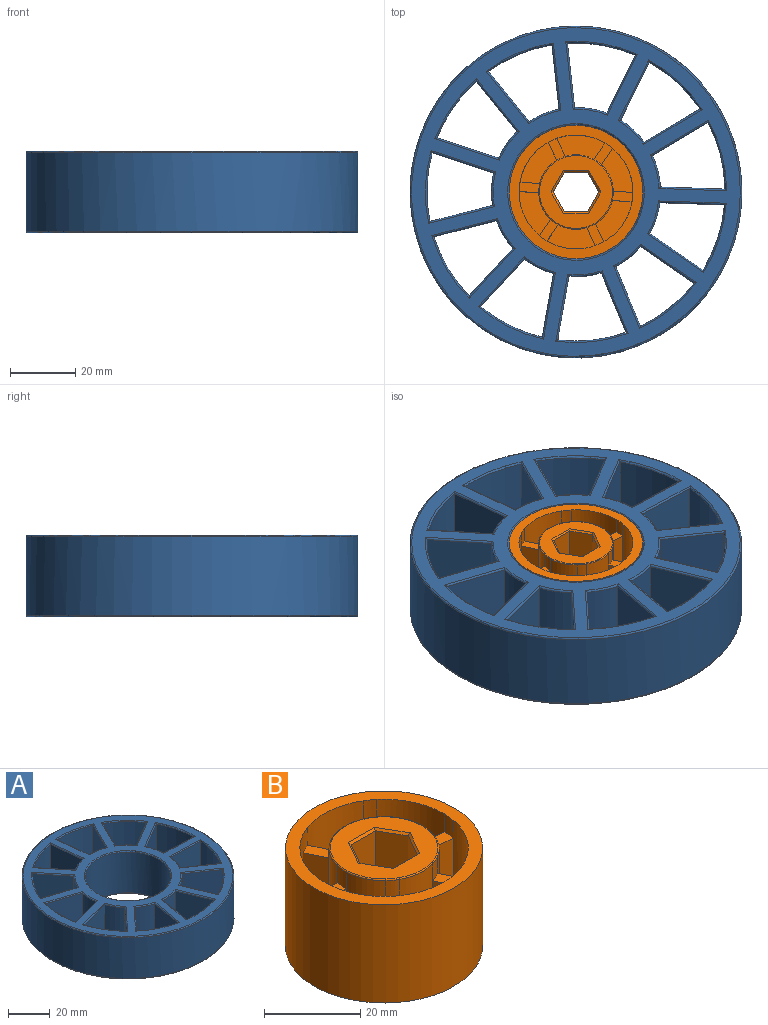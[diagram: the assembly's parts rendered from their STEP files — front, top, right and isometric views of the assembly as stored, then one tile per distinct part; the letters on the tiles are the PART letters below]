
ASSEMBLY  parts=2 mates=1
PART A: 140 faces, bbox 110.4x110.4x25 mm
  f0: plane 101x101mm, normal (0,0,1), area 2810.5mm2, adj f48,f49,f50,f51,f52,f53,f54,f55
  f1: plane 101x101mm, normal (0,0,-1), area 2810.5mm2, adj f94,f95,f96,f97,f98,f99,f100,f101
  f2: cylinder r=51mm len=102mm, axis (0,0,-1), area 7690.6mm2, adj f93,f139
  f3: cylinder r=20.5mm len=41mm, axis (0,0,-1), area 3091.3mm2, adj f92,f138
  f4: plane 24x16.33mm, normal (-0.57,-0.82,0), area 476.4mm2, adj f5,f7,f88,f137
  f5: cylinder r=26mm len=24mm, axis (0,0,1), area 240.4mm2, adj f4,f6,f89,f136
  f6: plane 24x18.32mm, normal (0.92,0.38,0), area 476.4mm2, adj f5,f7,f91,f134
  f7: cylinder r=45.8mm len=24mm, axis (0,0,1), area 512mm2, adj f4,f6,f90,f135
  f8: plane 24x18.85mm, normal (0.31,0.95,0), area 476.4mm2, adj f9,f11,f69,f133
  f9: cylinder r=26mm len=24mm, axis (0,0,1), area 240.4mm2, adj f8,f10,f68,f132
  f10: plane 24x15.43mm, normal (-0.78,-0.63,0), area 476.4mm2, adj f9,f11,f70,f130
  f11: cylinder r=45.8mm len=24mm, axis (0,0,1), area 512mm2, adj f8,f10,f71,f131
  f12: plane 24x19.73mm, normal (0.99,0.11,0), area 476.4mm2, adj f13,f15,f61,f129
  f13: cylinder r=26mm len=24mm, axis (0,0,1), area 240.4mm2, adj f12,f14,f60,f128
  f14: plane 24x17.77mm, normal (-0.9,0.45,0), area 476.4mm2, adj f13,f15,f62,f126
  f15: cylinder r=45.8mm len=24mm, axis (0,0,1), area 512mm2, adj f12,f14,f63,f127
  f16: plane 24x19.54mm, normal (-0.98,0.18,0), area 476.4mm2, adj f17,f19,f81,f125
  f17: cylinder r=26mm len=24mm, axis (0,0,1), area 240.4mm2, adj f16,f18,f80,f124
  f18: plane 24x14.56mm, normal (0.73,-0.68,0), area 476.4mm2, adj f17,f19,f82,f122
  f19: cylinder r=45.8mm len=24mm, axis (0,0,1), area 512mm2, adj f16,f18,f83,f123
  f20: plane 24x19.22mm, normal (-0.25,0.97,0), area 476.4mm2, adj f21,f23,f73,f121
  f21: cylinder r=26mm len=24mm, axis (0,0,1), area 240.4mm2, adj f20,f22,f72,f120
  f22: plane 24x18.85mm, normal (-0.31,-0.95,0), area 476.4mm2, adj f21,f23,f74,f118
  f23: cylinder r=45.8mm len=24mm, axis (0,0,1), area 512mm2, adj f20,f22,f75,f119
  f24: plane 24x15.43mm, normal (0.78,0.63,0), area 476.4mm2, adj f25,f27,f65,f117
  f25: cylinder r=26mm len=24mm, axis (0,0,1), area 240.4mm2, adj f24,f26,f64,f116
  f26: plane 24x19.73mm, normal (-0.99,-0.11,0), area 476.4mm2, adj f25,f27,f66,f114
  f27: cylinder r=45.8mm len=24mm, axis (0,0,1), area 512mm2, adj f24,f26,f67,f115
  f28: plane 24x17.77mm, normal (0.9,-0.45,0), area 476.4mm2, adj f29,f31,f57,f113
  f29: cylinder r=26mm len=24mm, axis (0,0,1), area 240.4mm2, adj f28,f30,f56,f112
  f30: plane 24x17.05mm, normal (-0.51,0.86,0), area 476.4mm2, adj f29,f31,f58,f110
  f31: cylinder r=45.8mm len=24mm, axis (0,0,1), area 512mm2, adj f28,f30,f59,f111
  f32: plane 24x19.84mm, normal (-0.03,-1,0), area 476.4mm2, adj f33,f35,f49,f109
  f33: cylinder r=26mm len=24mm, axis (0,0,1), area 240.4mm2, adj f32,f34,f48,f108
  f34: plane 24x16.33mm, normal (0.57,0.82,0), area 476.4mm2, adj f33,f35,f50,f106
  f35: cylinder r=45.8mm len=24mm, axis (0,0,1), area 512mm2, adj f32,f34,f51,f107
  f36: plane 24x17.05mm, normal (0.51,-0.86,0), area 476.4mm2, adj f37,f39,f53,f105
  f37: cylinder r=26mm len=24mm, axis (0,0,1), area 240.4mm2, adj f36,f38,f52,f104
  f38: plane 24x19.84mm, normal (0.03,1,0), area 476.4mm2, adj f37,f39,f54,f102
  f39: cylinder r=45.8mm len=24mm, axis (0,0,1), area 512mm2, adj f36,f38,f55,f103
  f40: plane 24x18.32mm, normal (-0.92,-0.38,0), area 476.4mm2, adj f41,f43,f85,f101
  f41: cylinder r=26mm len=24mm, axis (0,0,1), area 240.4mm2, adj f40,f42,f84,f100
  f42: plane 24x19.54mm, normal (0.98,-0.18,0), area 476.4mm2, adj f41,f43,f86,f98
  f43: cylinder r=45.8mm len=24mm, axis (0,0,1), area 512mm2, adj f40,f42,f87,f99
  f44: plane 24x14.56mm, normal (-0.73,0.68,0), area 476.4mm2, adj f45,f47,f77,f97
  f45: cylinder r=26mm len=24mm, axis (0,0,1), area 240.4mm2, adj f44,f46,f76,f96
  f46: plane 24x19.22mm, normal (0.25,-0.97,0), area 476.4mm2, adj f45,f47,f78,f94
  f47: cylinder r=45.8mm len=24mm, axis (0,0,1), area 512mm2, adj f44,f46,f79,f95
  f48: torus R=25.5mm, axis (0,0,1), area 8.1mm2, adj f0,f33,f49,f50
  f49: cylinder r=0.5mm len=20.84mm, axis (1,-0.03,0), area 15.9mm2, adj f0,f32,f48,f51
  f50: cylinder r=0.5mm len=17.42mm, axis (-0.82,0.57,0), area 15.9mm2, adj f0,f34,f48,f51
  f51: torus R=46.3mm, axis (0,0,1), area 17.1mm2, adj f0,f35,f49,f50
  f52: torus R=25.5mm, axis (0,0,1), area 8.1mm2, adj f0,f37,f53,f54
  f53: cylinder r=0.5mm len=18.15mm, axis (0.86,0.51,0), area 15.9mm2, adj f0,f36,f52,f55
  f54: cylinder r=0.5mm len=20.84mm, axis (-1,0.03,0), area 15.9mm2, adj f0,f38,f52,f55
  f55: torus R=46.3mm, axis (0,0,1), area 17.1mm2, adj f0,f39,f53,f54
  f56: torus R=25.5mm, axis (0,0,1), area 8.1mm2, adj f0,f29,f57,f58
  f57: cylinder r=0.5mm len=18.87mm, axis (0.45,0.9,0), area 15.9mm2, adj f0,f28,f56,f59
  f58: cylinder r=0.5mm len=18.15mm, axis (-0.86,-0.51,0), area 15.9mm2, adj f0,f30,f56,f59
  f59: torus R=46.3mm, axis (0,0,1), area 17.1mm2, adj f0,f31,f57,f58
  f60: torus R=25.5mm, axis (0,0,1), area 8.1mm2, adj f0,f13,f61,f62
  f61: cylinder r=0.5mm len=20.76mm, axis (-0.11,0.99,0), area 15.9mm2, adj f0,f12,f60,f63
  f62: cylinder r=0.5mm len=18.87mm, axis (-0.45,-0.9,0), area 15.9mm2, adj f0,f14,f60,f63
  f63: torus R=46.3mm, axis (0,0,1), area 17.1mm2, adj f0,f15,f61,f62
  f64: torus R=25.5mm, axis (0,0,1), area 8.1mm2, adj f0,f25,f65,f66
  f65: cylinder r=0.5mm len=16.51mm, axis (-0.63,0.78,0), area 15.9mm2, adj f0,f24,f64,f67
  f66: cylinder r=0.5mm len=20.76mm, axis (0.11,-0.99,0), area 15.9mm2, adj f0,f26,f64,f67
  f67: torus R=46.3mm, axis (0,0,1), area 17.1mm2, adj f0,f27,f65,f66
  f68: torus R=25.5mm, axis (0,0,1), area 8.1mm2, adj f0,f9,f69,f70
  f69: cylinder r=0.5mm len=19.94mm, axis (-0.95,0.31,0), area 15.9mm2, adj f0,f8,f68,f71
  f70: cylinder r=0.5mm len=16.51mm, axis (0.63,-0.78,0), area 15.9mm2, adj f0,f10,f68,f71
  f71: torus R=46.3mm, axis (0,0,1), area 17.1mm2, adj f0,f11,f69,f70
  f72: torus R=25.5mm, axis (0,0,1), area 8.1mm2, adj f0,f21,f73,f74
  f73: cylinder r=0.5mm len=20.3mm, axis (-0.97,-0.25,0), area 15.9mm2, adj f0,f20,f72,f75
  f74: cylinder r=0.5mm len=19.94mm, axis (0.95,-0.31,0), area 15.9mm2, adj f0,f22,f72,f75
  f75: torus R=46.3mm, axis (0,0,1), area 17.1mm2, adj f0,f23,f73,f74
  f76: torus R=25.5mm, axis (0,0,1), area 8.1mm2, adj f0,f45,f77,f78
  f77: cylinder r=0.5mm len=15.62mm, axis (-0.68,-0.73,0), area 15.9mm2, adj f0,f44,f76,f79
  f78: cylinder r=0.5mm len=20.3mm, axis (0.97,0.25,0), area 15.9mm2, adj f0,f46,f76,f79
  f79: torus R=46.3mm, axis (0,0,1), area 17.1mm2, adj f0,f47,f77,f78
  f80: torus R=25.5mm, axis (0,0,1), area 8.1mm2, adj f0,f17,f81,f82
  f81: cylinder r=0.5mm len=20.6mm, axis (-0.18,-0.98,0), area 15.9mm2, adj f0,f16,f80,f83
  f82: cylinder r=0.5mm len=15.62mm, axis (0.68,0.73,0), area 15.9mm2, adj f0,f18,f80,f83
  f83: torus R=46.3mm, axis (0,0,1), area 17.1mm2, adj f0,f19,f81,f82
  f84: torus R=25.5mm, axis (0,0,1), area 8.1mm2, adj f0,f41,f85,f86
  f85: cylinder r=0.5mm len=19.42mm, axis (0.38,-0.92,0), area 15.9mm2, adj f0,f40,f84,f87
  f86: cylinder r=0.5mm len=20.6mm, axis (0.18,0.98,0), area 15.9mm2, adj f0,f42,f84,f87
  f87: torus R=46.3mm, axis (0,0,1), area 17.1mm2, adj f0,f43,f85,f86
  f88: cylinder r=0.5mm len=17.42mm, axis (0.82,-0.57,0), area 15.9mm2, adj f0,f4,f89,f90
  f89: torus R=25.5mm, axis (0,0,1), area 8.1mm2, adj f0,f5,f88,f91
  f90: torus R=46.3mm, axis (0,0,1), area 17.1mm2, adj f0,f7,f88,f91
  f91: cylinder r=0.5mm len=19.42mm, axis (-0.38,0.92,0), area 15.9mm2, adj f0,f6,f89,f90
  f92: torus R=21mm, axis (0,0,1), area 102.1mm2, adj f0,f3
  f93: torus R=50.5mm, axis (0,0,1), area 250.8mm2, adj f0,f2
  f94: cylinder r=0.5mm len=20.3mm, axis (-0.97,-0.25,0), area 15.9mm2, adj f1,f46,f95,f96
  f95: torus R=46.3mm, axis (0,0,-1), area 17.1mm2, adj f1,f47,f94,f97
  f96: torus R=25.5mm, axis (0,0,-1), area 8.1mm2, adj f1,f45,f94,f97
  f97: cylinder r=0.5mm len=15.62mm, axis (0.68,0.73,0), area 15.9mm2, adj f1,f44,f95,f96
  f98: cylinder r=0.5mm len=20.6mm, axis (-0.18,-0.98,0), area 15.9mm2, adj f1,f42,f99,f100
  f99: torus R=46.3mm, axis (0,0,-1), area 17.1mm2, adj f1,f43,f98,f101
  f100: torus R=25.5mm, axis (0,0,-1), area 8.1mm2, adj f1,f41,f98,f101
  f101: cylinder r=0.5mm len=19.42mm, axis (-0.38,0.92,0), area 15.9mm2, adj f1,f40,f99,f100
  f102: cylinder r=0.5mm len=20.84mm, axis (1,-0.03,0), area 15.9mm2, adj f1,f38,f103,f104
  f103: torus R=46.3mm, axis (0,0,-1), area 17.1mm2, adj f1,f39,f102,f105
  f104: torus R=25.5mm, axis (0,0,-1), area 8.1mm2, adj f1,f37,f102,f105
  f105: cylinder r=0.5mm len=18.15mm, axis (-0.86,-0.51,0), area 15.9mm2, adj f1,f36,f103,f104
  f106: cylinder r=0.5mm len=17.42mm, axis (0.82,-0.57,0), area 15.9mm2, adj f1,f34,f107,f108
  f107: torus R=46.3mm, axis (0,0,-1), area 17.1mm2, adj f1,f35,f106,f109
  f108: torus R=25.5mm, axis (0,0,-1), area 8.1mm2, adj f1,f33,f106,f109
  f109: cylinder r=0.5mm len=20.84mm, axis (-1,0.03,0), area 15.9mm2, adj f1,f32,f107,f108
  f110: cylinder r=0.5mm len=18.15mm, axis (0.86,0.51,0), area 15.9mm2, adj f1,f30,f111,f112
  f111: torus R=46.3mm, axis (0,0,-1), area 17.1mm2, adj f1,f31,f110,f113
  f112: torus R=25.5mm, axis (0,0,-1), area 8.1mm2, adj f1,f29,f110,f113
  f113: cylinder r=0.5mm len=18.87mm, axis (-0.45,-0.9,0), area 15.9mm2, adj f1,f28,f111,f112
  f114: cylinder r=0.5mm len=20.76mm, axis (-0.11,0.99,0), area 15.9mm2, adj f1,f26,f115,f116
  f115: torus R=46.3mm, axis (0,0,-1), area 17.1mm2, adj f1,f27,f114,f117
  f116: torus R=25.5mm, axis (0,0,-1), area 8.1mm2, adj f1,f25,f114,f117
  f117: cylinder r=0.5mm len=16.51mm, axis (0.63,-0.78,0), area 15.9mm2, adj f1,f24,f115,f116
  f118: cylinder r=0.5mm len=19.94mm, axis (-0.95,0.31,0), area 15.9mm2, adj f1,f22,f119,f120
  f119: torus R=46.3mm, axis (0,0,-1), area 17.1mm2, adj f1,f23,f118,f121
  f120: torus R=25.5mm, axis (0,0,-1), area 8.1mm2, adj f1,f21,f118,f121
  f121: cylinder r=0.5mm len=20.3mm, axis (0.97,0.25,0), area 15.9mm2, adj f1,f20,f119,f120
  f122: cylinder r=0.5mm len=15.62mm, axis (-0.68,-0.73,0), area 15.9mm2, adj f1,f18,f123,f124
  f123: torus R=46.3mm, axis (0,0,-1), area 17.1mm2, adj f1,f19,f122,f125
  f124: torus R=25.5mm, axis (0,0,-1), area 8.1mm2, adj f1,f17,f122,f125
  f125: cylinder r=0.5mm len=20.6mm, axis (0.18,0.98,0), area 15.9mm2, adj f1,f16,f123,f124
  f126: cylinder r=0.5mm len=18.87mm, axis (0.45,0.9,0), area 15.9mm2, adj f1,f14,f127,f128
  f127: torus R=46.3mm, axis (0,0,-1), area 17.1mm2, adj f1,f15,f126,f129
  f128: torus R=25.5mm, axis (0,0,-1), area 8.1mm2, adj f1,f13,f126,f129
  f129: cylinder r=0.5mm len=20.76mm, axis (0.11,-0.99,0), area 15.9mm2, adj f1,f12,f127,f128
  f130: cylinder r=0.5mm len=16.51mm, axis (-0.63,0.78,0), area 15.9mm2, adj f1,f10,f131,f132
  f131: torus R=46.3mm, axis (0,0,-1), area 17.1mm2, adj f1,f11,f130,f133
  f132: torus R=25.5mm, axis (0,0,-1), area 8.1mm2, adj f1,f9,f130,f133
  f133: cylinder r=0.5mm len=19.94mm, axis (0.95,-0.31,0), area 15.9mm2, adj f1,f8,f131,f132
  f134: cylinder r=0.5mm len=19.42mm, axis (0.38,-0.92,0), area 15.9mm2, adj f1,f6,f135,f136
  f135: torus R=46.3mm, axis (0,0,-1), area 17.1mm2, adj f1,f7,f134,f137
  f136: torus R=25.5mm, axis (0,0,-1), area 8.1mm2, adj f1,f5,f134,f137
  f137: cylinder r=0.5mm len=17.42mm, axis (-0.82,0.57,0), area 15.9mm2, adj f1,f4,f135,f136
  f138: torus R=21mm, axis (0,0,-1), area 102.1mm2, adj f1,f3
  f139: torus R=50.5mm, axis (0,0,-1), area 250.8mm2, adj f1,f2
PART B: 82 faces, bbox 41x41x25 mm
  f0: plane 41x41mm, normal (0,0,-1), area 1167.1mm2, adj f39,f64,f65,f66,f67,f68,f69
  f1: plane 41.01x41.01mm, normal (0,0,1), area 358.2mm2, adj f15,f18,f21,f24,f27,f29,f39,f42
  f2: plane 17.43x5.02mm, normal (0.82,-0.57,0), area 106.2mm2, adj f15,f16,f30,f55
  f3: plane 17.43x5.01mm, normal (-0.82,0.57,0), area 105.8mm2, adj f26,f29,f31,f55
  f4: plane 17.43x5.5mm, normal (0.9,0.43,0), area 106.2mm2, adj f26,f29,f31,f52
  f5: plane 17.43x5.48mm, normal (-0.9,-0.43,0), area 105.8mm2, adj f23,f27,f28,f52
  f6: plane 17.43x6.06mm, normal (-0.08,-1,0), area 105.8mm2, adj f20,f24,f25,f49
  f7: plane 17.43x6.08mm, normal (0.08,1,0), area 106.2mm2, adj f23,f27,f28,f49
  f8: plane 17.43x5.01mm, normal (0.82,-0.57,0), area 105.8mm2, adj f17,f21,f22,f46
  f9: plane 17.43x5.02mm, normal (-0.82,0.57,0), area 106.2mm2, adj f20,f24,f25,f46
  f10: plane 17.43x5.48mm, normal (0.9,0.43,0), area 105.8mm2, adj f14,f18,f19,f43
  f11: plane 17.43x5.5mm, normal (-0.9,-0.43,0), area 106.2mm2, adj f17,f21,f22,f43
  f12: plane 17.43x6.06mm, normal (0.08,1,0), area 105.8mm2, adj f15,f16,f30,f40
  f13: plane 17.43x6.08mm, normal (-0.08,-1,0), area 106.2mm2, adj f14,f18,f19,f40
  f14: plane 12.66x11.25mm, normal (0,0,1), area 74.1mm2, adj f10,f13,f18,f19
  f15: cylinder r=17.5mm len=22mm, axis (0,0,-1), area 339.3mm2, adj f1,f2,f12,f30,f42,f56
  f16: cylinder r=11.45mm len=21.75mm, axis (0,0,-1), area 197.5mm2, adj f2,f12,f30,f41,f57,f74
  f17: plane 14.86x7.44mm, normal (0,0,1), area 74.1mm2, adj f8,f11,f21,f22
  f18: cylinder r=17.5mm len=22mm, axis (0,0,-1), area 339.3mm2, adj f1,f10,f13,f14,f42,f45
  f19: cylinder r=11.45mm len=21.75mm, axis (0,0,-1), area 197.5mm2, adj f10,f13,f14,f41,f44,f78
  f20: plane 13.56x9.68mm, normal (0,0,1), area 74.1mm2, adj f6,f9,f24,f25
  f21: cylinder r=17.5mm len=22mm, axis (0,0,-1), area 339.3mm2, adj f1,f8,f11,f17,f45,f48
  f22: cylinder r=11.45mm len=21.75mm, axis (0,0,-1), area 197.5mm2, adj f8,f11,f17,f44,f47,f81
  f23: plane 12.66x11.25mm, normal (0,0,1), area 74.1mm2, adj f5,f7,f27,f28
  f24: cylinder r=17.5mm len=22mm, axis (0,0,-1), area 339.3mm2, adj f1,f6,f9,f20,f48,f51
  f25: cylinder r=11.45mm len=21.75mm, axis (0,0,-1), area 197.5mm2, adj f6,f9,f20,f47,f50,f77
  f26: plane 14.86x7.44mm, normal (0,0,1), area 74.1mm2, adj f3,f4,f29,f31
  f27: cylinder r=17.5mm len=22mm, axis (0,0,-1), area 339.3mm2, adj f1,f5,f7,f23,f51,f54
  f28: cylinder r=11.45mm len=21.75mm, axis (0,0,-1), area 197.5mm2, adj f5,f7,f23,f50,f53,f73
  f29: cylinder r=17.5mm len=22mm, axis (0,0,-1), area 339.3mm2, adj f1,f3,f4,f26,f54,f56
  f30: plane 13.56x9.68mm, normal (0,0,1), area 74.1mm2, adj f2,f12,f15,f16
  f31: cylinder r=11.45mm len=21.75mm, axis (0,0,-1), area 197.5mm2, adj f3,f4,f26,f53,f57,f70
  f32: plane 22.39x22.38mm, normal (0,0,1), area 240.6mm2, adj f58,f59,f60,f61,f62,f63,f70,f71
  f33: plane 24x6.15mm, normal (0.87,0.5,0), area 170.4mm2, adj f34,f38,f59,f68
  f34: plane 24x7.1mm, normal (0,1,0), area 170.4mm2, adj f33,f35,f58,f69
  f35: plane 24x6.15mm, normal (-0.87,0.5,0), area 170.4mm2, adj f34,f36,f60,f67
  f36: plane 24x6.15mm, normal (-0.87,-0.5,0), area 170.4mm2, adj f35,f37,f62,f65
  f37: plane 24x7.1mm, normal (0,-1,0), area 170.4mm2, adj f36,f38,f63,f64
  f38: plane 24x6.15mm, normal (0.87,-0.5,0), area 170.4mm2, adj f33,f37,f61,f66
  f39: cylinder r=20.5mm len=41mm, axis (0,0,-1), area 3220.1mm2, adj f0,f1
  f40: plane 6.35x3.37mm, normal (0,0,1), area 17.6mm2, adj f12,f13,f41,f42
  f41: cylinder r=11.44mm len=4.32mm, axis (0,0,1), area 12.6mm2, adj f16,f19,f40,f76
  f42: cylinder r=17.5mm len=4.57mm, axis (0,0,1), area 13.3mm2, adj f1,f15,f18,f40
  f43: plane 6.7x5.26mm, normal (0,0,1), area 17.6mm2, adj f10,f11,f44,f45
  f44: cylinder r=11.44mm len=4.32mm, axis (0,0,1), area 12.6mm2, adj f19,f22,f43,f80
  f45: cylinder r=17.5mm len=4.57mm, axis (0,0,1), area 13.3mm2, adj f1,f18,f21,f43
  f46: plane 6.7x5.81mm, normal (0,0,1), area 17.6mm2, adj f8,f9,f47,f48
  f47: cylinder r=11.44mm len=4.32mm, axis (0,0,1), area 12.6mm2, adj f22,f25,f46,f79
  f48: cylinder r=17.5mm len=4.57mm, axis (0,0,1), area 13.3mm2, adj f1,f21,f24,f46
  f49: plane 6.35x3.37mm, normal (0,0,1), area 17.6mm2, adj f6,f7,f50,f51
  f50: cylinder r=11.44mm len=4.32mm, axis (0,0,1), area 12.6mm2, adj f25,f28,f49,f75
  f51: cylinder r=17.5mm len=4.57mm, axis (0,0,1), area 13.3mm2, adj f1,f24,f27,f49
  f52: plane 6.7x5.26mm, normal (0,0,1), area 17.6mm2, adj f4,f5,f53,f54
  f53: cylinder r=11.44mm len=4.32mm, axis (0,0,1), area 12.6mm2, adj f28,f31,f52,f71
  f54: cylinder r=17.5mm len=4.57mm, axis (0,0,1), area 13.3mm2, adj f1,f27,f29,f52
  f55: plane 6.7x5.81mm, normal (0,0,1), area 17.6mm2, adj f2,f3,f56,f57
  f56: cylinder r=17.5mm len=4.57mm, axis (0,0,1), area 13.3mm2, adj f1,f15,f29,f55
  f57: cylinder r=11.44mm len=4.32mm, axis (0,0,1), area 12.6mm2, adj f16,f31,f55,f72
  f58: plane 7.68x0.5mm, normal (0,0.71,0.71), area 5.2mm2, adj f32,f34,f59,f60
  f59: plane 6.65x4.13mm, normal (0.61,0.35,0.71), area 5.2mm2, adj f32,f33,f58,f61
  f60: plane 6.65x4.13mm, normal (-0.61,0.35,0.71), area 5.2mm2, adj f32,f35,f58,f62
  f61: plane 6.65x4.13mm, normal (0.61,-0.35,0.71), area 5.2mm2, adj f32,f38,f59,f63
  f62: plane 6.65x4.13mm, normal (-0.61,-0.35,0.71), area 5.2mm2, adj f32,f36,f60,f63
  f63: plane 7.68x0.5mm, normal (0,-0.71,0.71), area 5.2mm2, adj f32,f37,f61,f62
  f64: plane 7.68x0.5mm, normal (0,-0.71,-0.71), area 5.2mm2, adj f0,f37,f65,f66
  f65: plane 6.65x4.13mm, normal (-0.61,-0.35,-0.71), area 5.2mm2, adj f0,f36,f64,f67
  f66: plane 6.65x4.13mm, normal (0.61,-0.35,-0.71), area 5.2mm2, adj f0,f38,f64,f68
  f67: plane 6.65x4.13mm, normal (-0.61,0.35,-0.71), area 5.2mm2, adj f0,f35,f65,f69
  f68: plane 6.65x4.13mm, normal (0.61,0.35,-0.71), area 5.2mm2, adj f0,f33,f66,f69
  f69: plane 7.68x0.5mm, normal (0,0.71,-0.71), area 5.2mm2, adj f0,f34,f67,f68
  f70: torus R=11.2mm, axis (0,0,1), area 3.6mm2, adj f31,f32,f71,f72
  f71: torus R=11.19mm, axis (0,0,1), area 1.1mm2, adj f32,f53,f70,f73
  f72: torus R=11.19mm, axis (0,0,1), area 1.1mm2, adj f32,f57,f70,f74
  f73: torus R=11.2mm, axis (0,0,1), area 3.6mm2, adj f28,f32,f71,f75
  f74: torus R=11.2mm, axis (0,0,1), area 3.6mm2, adj f16,f32,f72,f76
  f75: torus R=11.19mm, axis (0,0,1), area 1.1mm2, adj f32,f50,f73,f77
  f76: torus R=11.19mm, axis (0,0,1), area 1.1mm2, adj f32,f41,f74,f78
  f77: torus R=11.2mm, axis (0,0,1), area 3.6mm2, adj f25,f32,f75,f79
  f78: torus R=11.2mm, axis (0,0,1), area 3.6mm2, adj f19,f32,f76,f80
  f79: torus R=11.19mm, axis (0,0,1), area 1.1mm2, adj f32,f47,f77,f81
  f80: torus R=11.19mm, axis (0,0,1), area 1.1mm2, adj f32,f44,f78,f81
  f81: torus R=11.2mm, axis (0,0,1), area 3.6mm2, adj f22,f32,f79,f80
PLACE A at identity
PLACE B at identity fixed
MATE fastened A.f11 <-> B.f39  axis (0,0,-1) through (0,0,-3)mm
